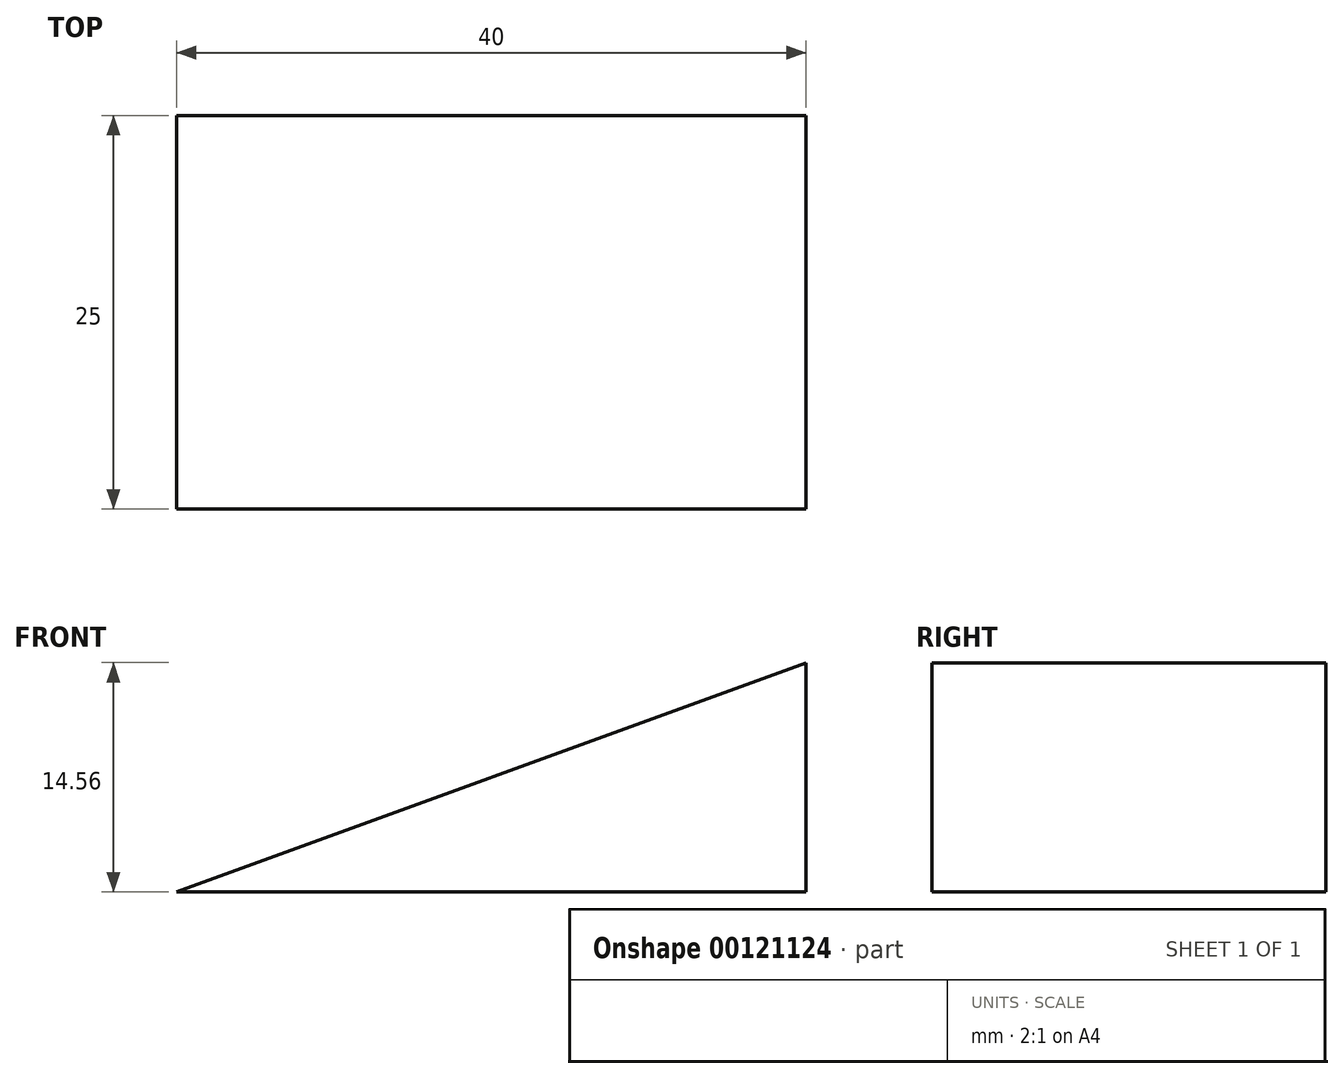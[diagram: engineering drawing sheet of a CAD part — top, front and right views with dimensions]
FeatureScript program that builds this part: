
annotation { "Feature Type Name" : "Feature", "Feature Type Description" : "" }
export const myFeature = defineFeature(function(context is Context, id is Id, definition is map)
    precondition{}
    {
        {
            var Q0;
            Q0=qCreatedBy(makeId("Front.planeOp"),FACE);
            var sketch = newSketch(context, id + "F0", { "sketchPlane" : qUnion([Q0])});
            skLineSegment(sketch, "E0", {"start": v(-20, 0) * mm, "end": v(20, 0) * mm});
            skLineSegment(sketch, "E1", {"start": v(20, 0) * mm, "end": v(20, 14.56) * mm});
            skLineSegment(sketch, "E2", {"start": v(20, 14.56) * mm, "end": v(-20, 0) * mm});
            skSolve(sketch);
        }
        {
            var Q0;
            Q0=makeQuery(id+"F0.imprint","IMPRINT",FACE,{"disambiguationData":[TD([[makeQuery(id+"F0.imprint","IMPRINT",EDGE,{"derivedFrom":sQuery(id+"F0.wireOp",EDGE,"E0")}),1.0]])]});
            extrude(context, id + "F1", {"entities" : qUnion([Q0]), "depth" : 25 * mm});
        }
    });
